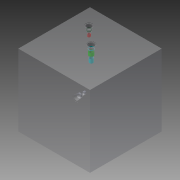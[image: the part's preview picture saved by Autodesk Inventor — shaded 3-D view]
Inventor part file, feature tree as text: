
AUTODESK INVENTOR PART (.ipt)
format: ipt  version: 2014 (Build 180170000, 170)  size: 268,288 bytes
history: native  units: mm
features: other x55, sketch x11, extrude x1
ambient origin geometry x8: Origin, YZ Plane, XZ Plane, XY Plane, X Axis, Y Axis, Z Axis, Center Point
bodies: 实体1 (feature_tree)
feature tree (67):
  extrude  "拉伸1"  TaperAngle=0.0deg  [1 undecoded]
  other  "UCS1"
  other  "UCS2"
  other  "UCS3"
  other  "UCS4"
  other  "UCS5"
  other  "UCS6"
  sketch  "草图1"  dims[d0=300.0mm d1=0.0mm]
  sketch  "草图7"  dims[d8=0.0mm d9=0.0mm d10=0.0mm d11=0.0mm d12=0.0mm d13=0.0mm]
  other  "曲面3"
  sketch  "草图8"  dims[d14=0.0mm d15=0.0mm d16=0.0mm d17=0.0mm d18=0.0mm d19=0.0mm]
  other  "曲面4"
  sketch  "草图9"  dims[d20=0.0mm d21=0.0mm d22=0.0mm d23=0.0mm d24=0.0mm d25=0.0mm]
  other  "曲面5"
  sketch  "草图11"  dims[d32=0.0mm d33=0.0mm d34=0.0mm d35=0.0mm d36=0.0mm d37=0.0mm d38=0.0mm]
  other  "曲面6"
  sketch  "草图12"  dims[d45=0.0mm]
  other  "曲面7"
  sketch  "草图14"  dims[d53=0.0mm]
  other  "曲面8"
  sketch  "草图15"  dims[d57=-48.42mm d58=0.13mm d59=0.0mm d60=-31.75mm d61=13.5mm d62=0.0mm d63=-15.07mm d64=3.18mm d65=0.0mm d66=0.0mm d70=-30.09mm d71=0.13mm d72=0.0mm d73=-15.07mm d74=6.35mm d75=0.0mm d76=0.0mm d80=-30.09mm d81=0.13mm d82=0.0mm d83=-15.07mm d84=6.35mm d85=0.0mm]
  other  "曲面9"
  other  "UCS1: YZ 平面"
  other  "UCS1: XZ 平面"
  other  "UCS1: XY 平面"
  other  "UCS1: X 轴"
  other  "UCS1: Y 轴"
  other  "UCS1: Z 轴"
  other  "UCS1: 原点"
  other  "UCS2: YZ 平面"
  other  "UCS2: XZ 平面"
  other  "UCS2: XY 平面"
  other  "UCS2: X 轴"
  other  "UCS2: Y 轴"
  other  "UCS2: Z 轴"
  other  "UCS2: 原点"
  other  "UCS3: YZ 平面"
  other  "UCS3: XZ 平面"
  other  "UCS3: XY 平面"
  other  "UCS3: X 轴"
  other  "UCS3: Y 轴"
  other  "UCS3: Z 轴"
  other  "UCS3: 原点"
  other  "UCS4: YZ 平面"
  other  "UCS4: XZ 平面"
  other  "UCS4: XY 平面"
  other  "UCS4: X 轴"
  other  "UCS4: Y 轴"
  other  "UCS4: Z 轴"
  other  "UCS4: 原点"
  other  "UCS5: YZ 平面"
  other  "UCS5: XZ 平面"
  other  "UCS5: XY 平面"
  other  "UCS5: X 轴"
  other  "UCS5: Y 轴"
  other  "UCS5: Z 轴"
  other  "UCS5: 原点"
  other  "UCS6: YZ 平面"
  other  "UCS6: XZ 平面"
  other  "UCS6: XY 平面"
  other  "UCS6: X 轴"
  other  "UCS6: Y 轴"
  other  "UCS6: Z 轴"
  other  "UCS6: 原点"
  sketch  "草图6"  dims[d2=0.0mm d3=0.0mm d4=0.0mm d5=0.0mm d6=0.0mm d7=0.0mm]
  sketch  "草图10"  dims[d26=0.0mm d27=0.0mm d28=0.0mm d29=0.0mm d30=0.0mm d31=0.0mm]
  sketch  "草图13"  dims[d52=0.0mm]
note: 1 required parameter value undecoded (feature->parameter linkage not recoverable at this tier; creation-order binding heuristic only, values carry confidence <= 0.55)
